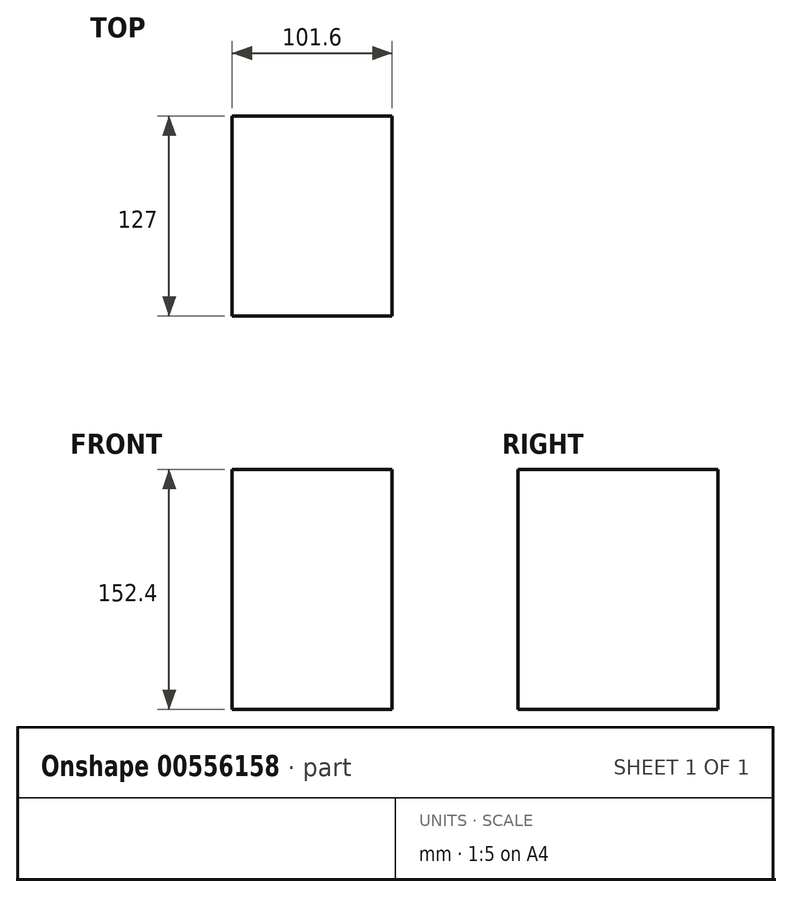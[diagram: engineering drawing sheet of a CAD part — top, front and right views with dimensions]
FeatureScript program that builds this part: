
annotation { "Feature Type Name" : "Feature", "Feature Type Description" : "" }
export const myFeature = defineFeature(function(context is Context, id is Id, definition is map)
    precondition{}
    {
        {
            var Q0;
            Q0=qCreatedBy(makeId("Top.planeOp"),FACE);
            var sketch = newSketch(context, id + "F0", { "sketchPlane" : qUnion([Q0])});
            skLineSegment(sketch, "E0.bottom", {"start": v(-101.6, 127) * mm, "end": v(0, 127) * mm});
            skLineSegment(sketch, "E0.top", {"start": v(-101.6, 0) * mm, "end": v(0, 0) * mm});
            skLineSegment(sketch, "E0.left", {"start": v(-101.6, 127) * mm, "end": v(-101.6, 0) * mm});
            skLineSegment(sketch, "E0.right", {"start": v(0, 127) * mm, "end": v(0, 0) * mm});
            skSolve(sketch);
        }
        {
            var Q0;
            Q0 = qSketchRegion(id + "F0", true);
            extrude(context, id + "F1", {"entities" : qUnion([Q0]), "depth" : 152.4 * mm, "offsetDistance" : 25.4 * mm});
        }
    });
